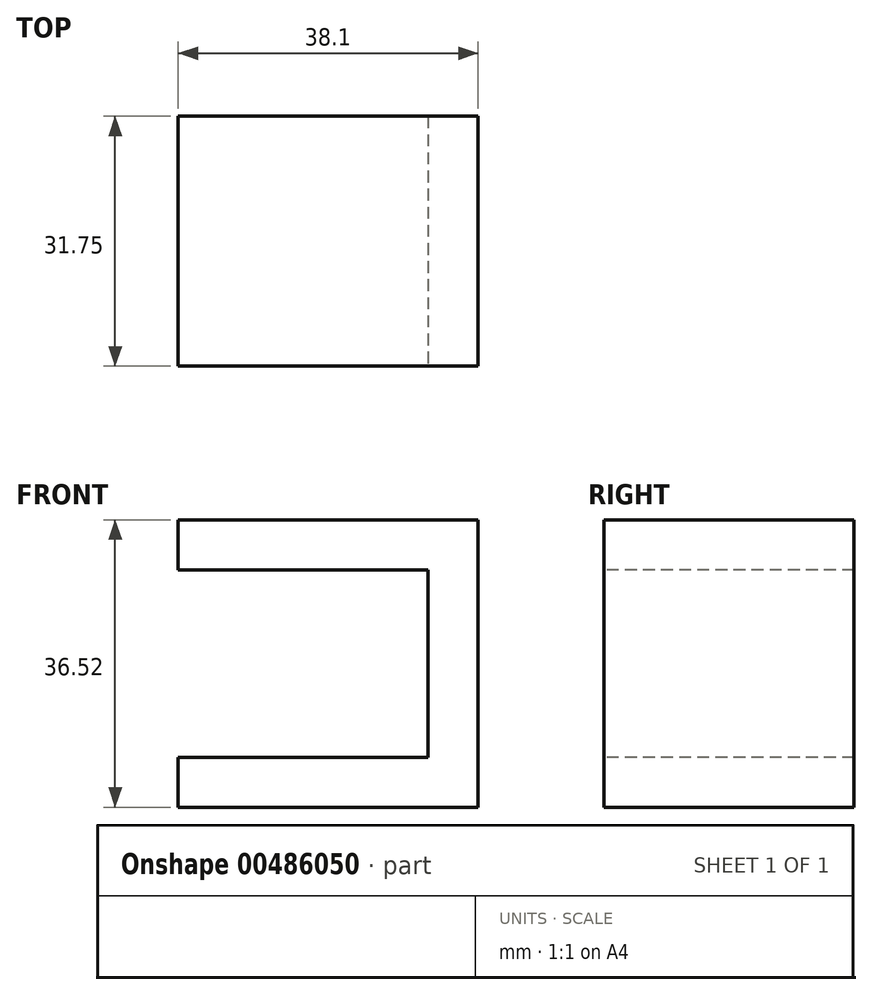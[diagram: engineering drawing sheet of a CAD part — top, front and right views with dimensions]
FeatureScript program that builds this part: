
annotation { "Feature Type Name" : "Feature", "Feature Type Description" : "" }
export const myFeature = defineFeature(function(context is Context, id is Id, definition is map)
    precondition{}
    {
        {
            var Q0;
            Q0=qCreatedBy(makeId("Front.planeOp"),FACE);
            var sketch = newSketch(context, id + "F0", { "sketchPlane" : qUnion([Q0])});
            skLineSegment(sketch, "E0", {"start": v(-49.93, 46.36) * mm, "end": v(-11.83, 46.36) * mm});
            skLineSegment(sketch, "E1", {"start": v(-49.93, 46.36) * mm, "end": v(-49.93, 40) * mm});
            skLineSegment(sketch, "E2", {"start": v(-11.83, 46.36) * mm, "end": v(-11.83, 9.84) * mm});
            skLineSegment(sketch, "E3", {"start": v(-11.83, 9.84) * mm, "end": v(-49.93, 9.84) * mm});
            skLineSegment(sketch, "E4", {"start": v(-49.93, 9.84) * mm, "end": v(-49.93, 16.2) * mm});
            skLineSegment(sketch, "E5", {"start": v(-49.93, 16.2) * mm, "end": v(-18.18, 16.2) * mm});
            skLineSegment(sketch, "E6", {"start": v(-49.93, 40) * mm, "end": v(-18.18, 40) * mm});
            skLineSegment(sketch, "E7", {"start": v(-18.18, 40) * mm, "end": v(-18.18, 16.2) * mm});
            skSolve(sketch);
        }
        {
            var Q0;
            Q0=makeQuery(id+"F0.imprint","IMPRINT",FACE,{"disambiguationData":[TD([[makeQuery(id+"F0.imprint","IMPRINT",EDGE,{"derivedFrom":sQuery(id+"F0.wireOp",EDGE,"E0")}),-1.0]])]});
            extrude(context, id + "F1", {"entities" : qUnion([Q0]), "oppositeDirection" : true, "depth" : 31.75 * mm});
        }
    });
